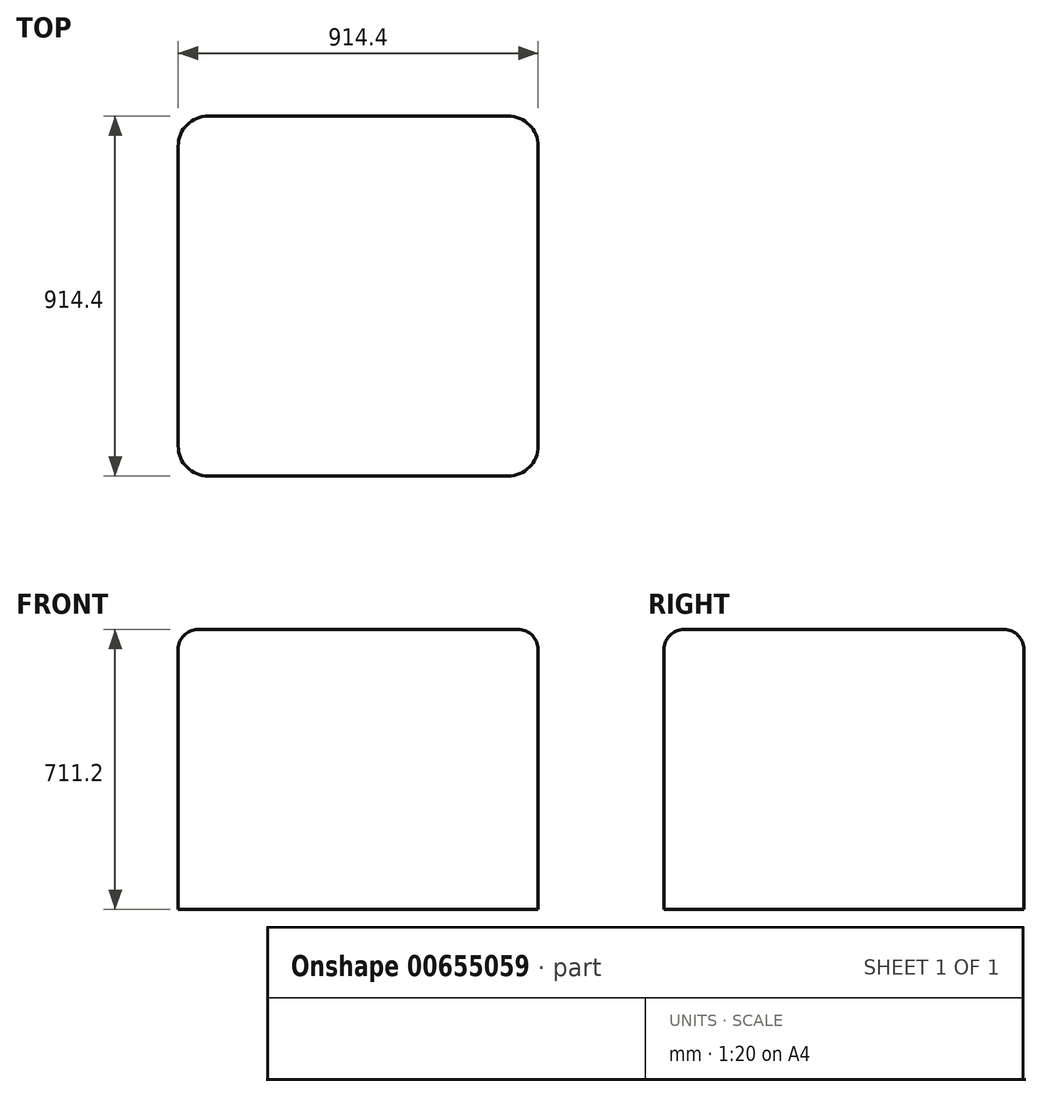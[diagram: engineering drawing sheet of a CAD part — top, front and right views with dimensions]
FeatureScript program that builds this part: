
annotation { "Feature Type Name" : "Feature", "Feature Type Description" : "" }
export const myFeature = defineFeature(function(context is Context, id is Id, definition is map)
    precondition{}
    {
        {
            var Q0;
            Q0=qCreatedBy(makeId("Top.planeOp"),FACE);
            var sketch = newSketch(context, id + "F0", { "sketchPlane" : qUnion([Q0])});
            skLineSegment(sketch, "E0", {"start": v(-241.3, -215.9) * mm, "end": v(-241.3, -1130.3) * mm});
            skLineSegment(sketch, "E1", {"start": v(-241.3, -1130.3) * mm, "end": v(-1155.7, -1130.3) * mm});
            skLineSegment(sketch, "E2", {"start": v(-1155.7, -1130.3) * mm, "end": v(-1155.7, -215.9) * mm});
            skLineSegment(sketch, "E3", {"start": v(-1155.7, -215.9) * mm, "end": v(-241.3, -215.9) * mm});
            skSolve(sketch);
        }
        {
            var Q0;
            Q0=makeQuery(id+"F0.imprint","IMPRINT",FACE,{"disambiguationData":[TD([[makeQuery(id+"F0.imprint","IMPRINT",EDGE,{"derivedFrom":sQuery(id+"F0.wireOp",EDGE,"E0")}),-1.0]])]});
            extrude(context, id + "F1", {"entities" : qUnion([Q0]), "depth" : 711.2 * mm, "offsetDistance" : 25.4 * mm});
        }
        {
            var Q0;
            Q0=makeQuery(id+"F1.opExtrude","SWEPT_EDGE",EDGE,{"disambiguationData":[OSD([sQuery(id+"F0.wireOp",EDGE,"E1"),sQuery(id+"F0.wireOp",EDGE,"E2")])]});
            var Q1;
            Q1=makeQuery(id+"F1.opExtrude","SWEPT_EDGE",EDGE,{"disambiguationData":[OSD([sQuery(id+"F0.wireOp",EDGE,"E2"),sQuery(id+"F0.wireOp",EDGE,"E3")])]});
            var Q2;
            Q2=makeQuery(id+"F1.opExtrude","SWEPT_EDGE",EDGE,{"disambiguationData":[OSD([sQuery(id+"F0.wireOp",EDGE,"E0"),sQuery(id+"F0.wireOp",EDGE,"E1")])]});
            var Q3;
            Q3=makeQuery(id+"F1.opExtrude","SWEPT_EDGE",EDGE,{"disambiguationData":[OSD([sQuery(id+"F0.wireOp",EDGE,"E0"),sQuery(id+"F0.wireOp",EDGE,"E3")])]});
            fillet(context, id + "F2", {"entities" : qUnion([Q0, Q1, Q2, Q3]), "radius" : 76.2 * mm, "tangentPropagation" : true, "allowEdgeOverflow" : false});
        }
        {
            var Q0;
            Q0=makeQuery(id+"F1.opExtrude","CAP_EDGE",EDGE,{"disambiguationData":[OSD([sQuery(id+"F0.wireOp",EDGE,"E1")])],"isStart":false});
            fillet(context, id + "F3", {"entities" : qUnion([Q0]), "radius" : 50.8 * mm, "tangentPropagation" : true, "allowEdgeOverflow" : false});
        }
    });
